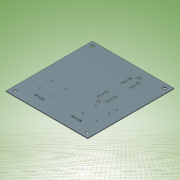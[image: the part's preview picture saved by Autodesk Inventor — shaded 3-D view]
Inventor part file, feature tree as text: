
AUTODESK INVENTOR PART (.ipt)
format: ipt  version: 2022 (Build 260153000, 153)  size: 289,280 bytes
history: native  units: mm
features: other x1, extrude x1, sketch x1
ambient origin geometry x8: Origin, YZ Plane, XZ Plane, XY Plane, X Axis, Y Axis, Z Axis, Center Point
bodies: Body1 (feature_tree)
feature tree (3):
  other  "Sólido1"
  extrude  "Extrusión1"  Depth=370.0mm
  sketch  "Boceto1"  dims[d0=350.0mm d1=370.0mm d2=3.0mm d3=0.0mm d4=12.0mm d5=20.0mm d6=20.0mm d7=5.0mm d8=5.0mm d11=10.0mm d12=6.0mm d13=10.0mm d15=18.0mm d16=6.0mm d17=9.011mm d18=10.0mm d19=6.0mm d20=10.0mm d21=6.0mm d22=18.0mm d23=9.011mm d26=121.023mm d27=45.0mm d29=15.0mm d30=250.0mm d31=5.0mm d33=10.0mm d34=6.0mm d35=10.0mm d36=20.0mm d37=10.0mm d39=10.0mm d40=60.0mm d41=6.0mm d42=5.0mm d43=10.0mm d44=6.0mm d45=10.0mm d46=20.0mm d48=10.0mm d50=42.0mm d51=6.0mm d52=6.0mm d53=5.0mm d54=6.0mm d55=10.0mm d56=5.0mm d57=20.0mm d58=10.0mm d59=6.0mm d60=10.0mm d61=10.0mm d62=6.0mm d64=16.0mm d66=10.0mm d67=6.0mm d68=16.0mm d70=20.0mm d71=20.0mm d73=20.0mm d77=20.0mm d81=65.0mm d82=60.0mm d83=5.0mm d84=11.34178mm d85=48.0mm d86=4.0mm d87=3.683mm d88=2.921mm d89=4.0mm d90=3.556mm d91=2.921mm d92=4.0mm d93=3.556mm d94=3.683mm d95=4.0mm d96=3.683mm d97=3.683mm d98=80.0mm d99=65.0mm d100=60.0mm d101=4.0mm d102=3.683mm d103=2.921mm d104=4.0mm d105=3.556mm d106=2.921mm d107=4.0mm d108=3.556mm d109=3.683mm d110=4.0mm d111=3.683mm d112=3.683mm d113=120.0mm]
